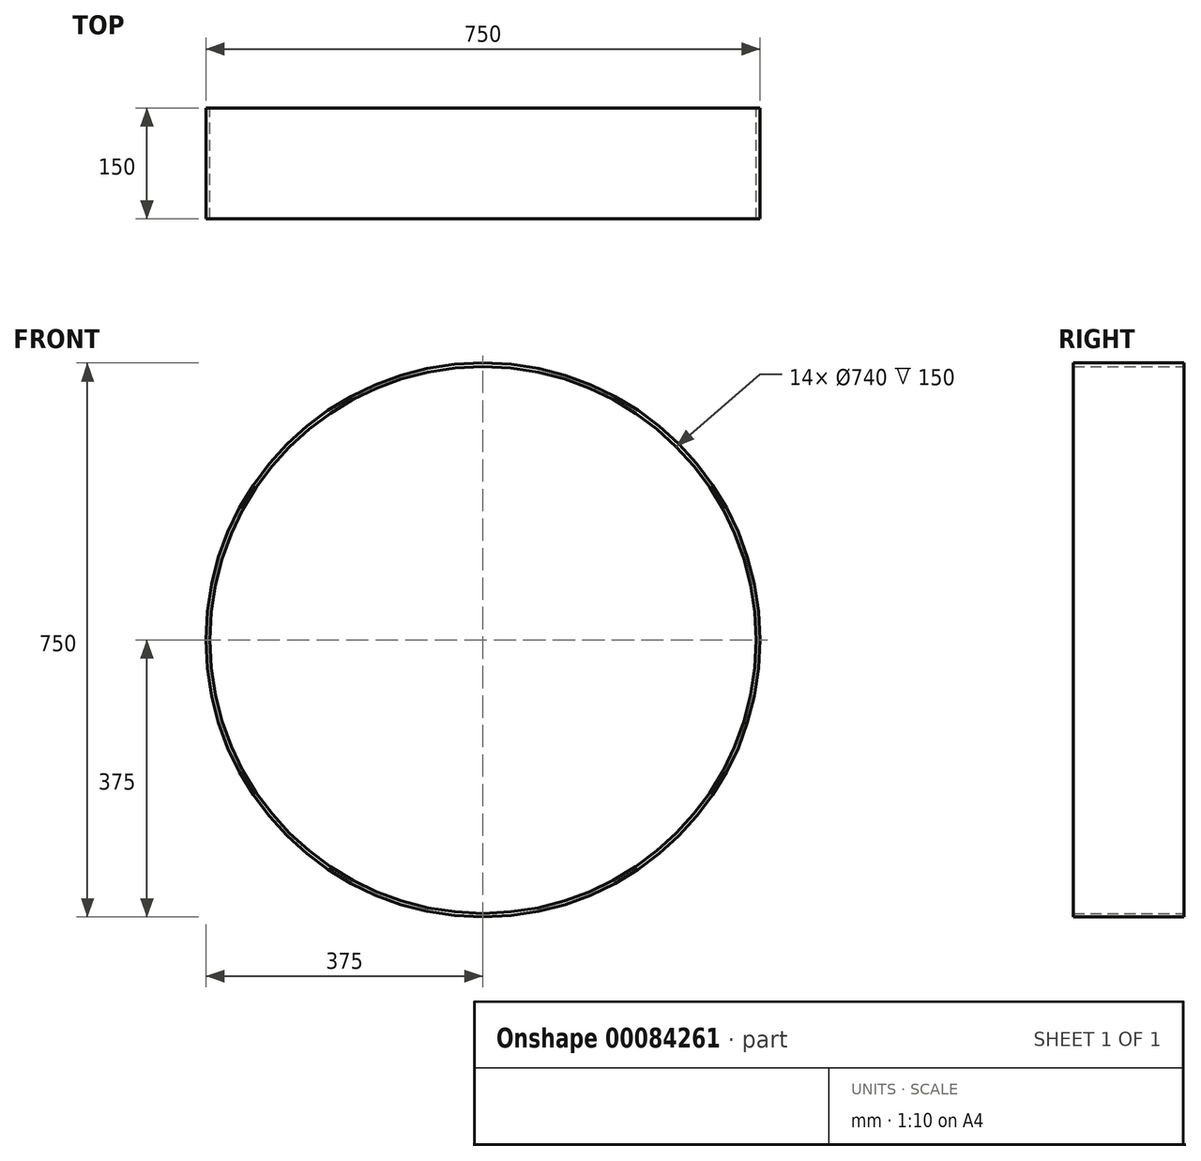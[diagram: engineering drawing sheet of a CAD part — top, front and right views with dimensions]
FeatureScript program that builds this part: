
annotation { "Feature Type Name" : "Feature", "Feature Type Description" : "" }
export const myFeature = defineFeature(function(context is Context, id is Id, definition is map)
    precondition{}
    {
        {
            var Q0;
            Q0=qCreatedBy(makeId("Front.planeOp"),FACE);
            var sketch = newSketch(context, id + "F0", { "sketchPlane" : qUnion([Q0])});
            skCircle(sketch, "E0", {"center": v(0, 0) * mm, "radius": 375 * mm});
            skSolve(sketch);
        }
        {
            var Q0;
            Q0=makeQuery(id+"F0.imprint","IMPRINT",FACE,{"disambiguationData":[TD([[makeQuery(id+"F0.imprint","IMPRINT",EDGE,{"derivedFrom":sQuery(id+"F0.wireOp",EDGE,"E0")}),1.0]])]});
            var sketch = newSketch(context, id + "F1", { "sketchPlane" : qUnion([Q0])});
            skCircle(sketch, "E1", {"center": v(0, 0) * mm, "radius": 370 * mm});
            skSolve(sketch);
        }
        {
            var Q0;
            Q0=makeQuery(id+"F0.imprint","IMPRINT",FACE,{"disambiguationData":[TD([[makeQuery(id+"F0.imprint","IMPRINT",EDGE,{"derivedFrom":sQuery(id+"F0.wireOp",EDGE,"E0")}),1.0]])]});
            var sketch = newSketch(context, id + "F2", { "sketchPlane" : qUnion([Q0])});
            skCircle(sketch, "E2", {"center": v(0, 0) * mm, "radius": 365 * mm, "construction": true});
            skCircle(sketch, "E3", {"center": v(14.62, 364.7) * mm, "radius": 5 * mm});
            skSolve(sketch);
        }
        {
            var Q0;
            Q0=sQuery(id+"F2.wireOp",EDGE,"E3");
            extrude(context, id + "F3", {"bodyType" : ToolBodyType.SURFACE, "surfaceEntities" : qUnion([Q0]), "depth" : 2500 * mm});
        }
        {
            var Q0;
            Q0=makeQuery(id+"F3.opExtrude","SWEPT_BODY",BODY,{"disambiguationData":[OSD([sQuery(id+"F2.wireOp",EDGE,"E3")])]});
            var Q1;
            Q1=sQuery(id+"F1.wireOp",EDGE,"E1");
            circularPattern(context, id + "F4", {"entities" : qUnion([Q0]), "axis" : qUnion([Q1]), "angle" : 360 * degree, "instanceCount" : 45, "equalSpace" : true});
        }
        {
            var Q0;
            Q0=makeQuery(id+"F0.imprint","IMPRINT",FACE,{"disambiguationData":[TD([[makeQuery(id+"F0.imprint","IMPRINT",EDGE,{"derivedFrom":sQuery(id+"F0.wireOp",EDGE,"E0")}),1.0]])]});
            var sketch = newSketch(context, id + "F5", { "sketchPlane" : qUnion([Q0])});
            skCircle(sketch, "E4", {"center": v(0, 0) * mm, "radius": 370 * mm});
            skCircle(sketch, "E5", {"center": v(0, 0) * mm, "radius": 375 * mm});
            skSolve(sketch);
        }
        {
            var Q0;
            Q0 = qSketchRegion(id + "F5", true);
            var Q1;
            Q1=makeQuery(id+"F0.imprint","IMPRINT",FACE,{"disambiguationData":[TD([[makeQuery(id+"F0.imprint","IMPRINT",EDGE,{"derivedFrom":sQuery(id+"F0.wireOp",EDGE,"E0")}),1.0]])]});
            extrude(context, id + "F6", {"entities" : qUnion([Q0, Q1]), "depth" : 150 * mm});
        }
    });
